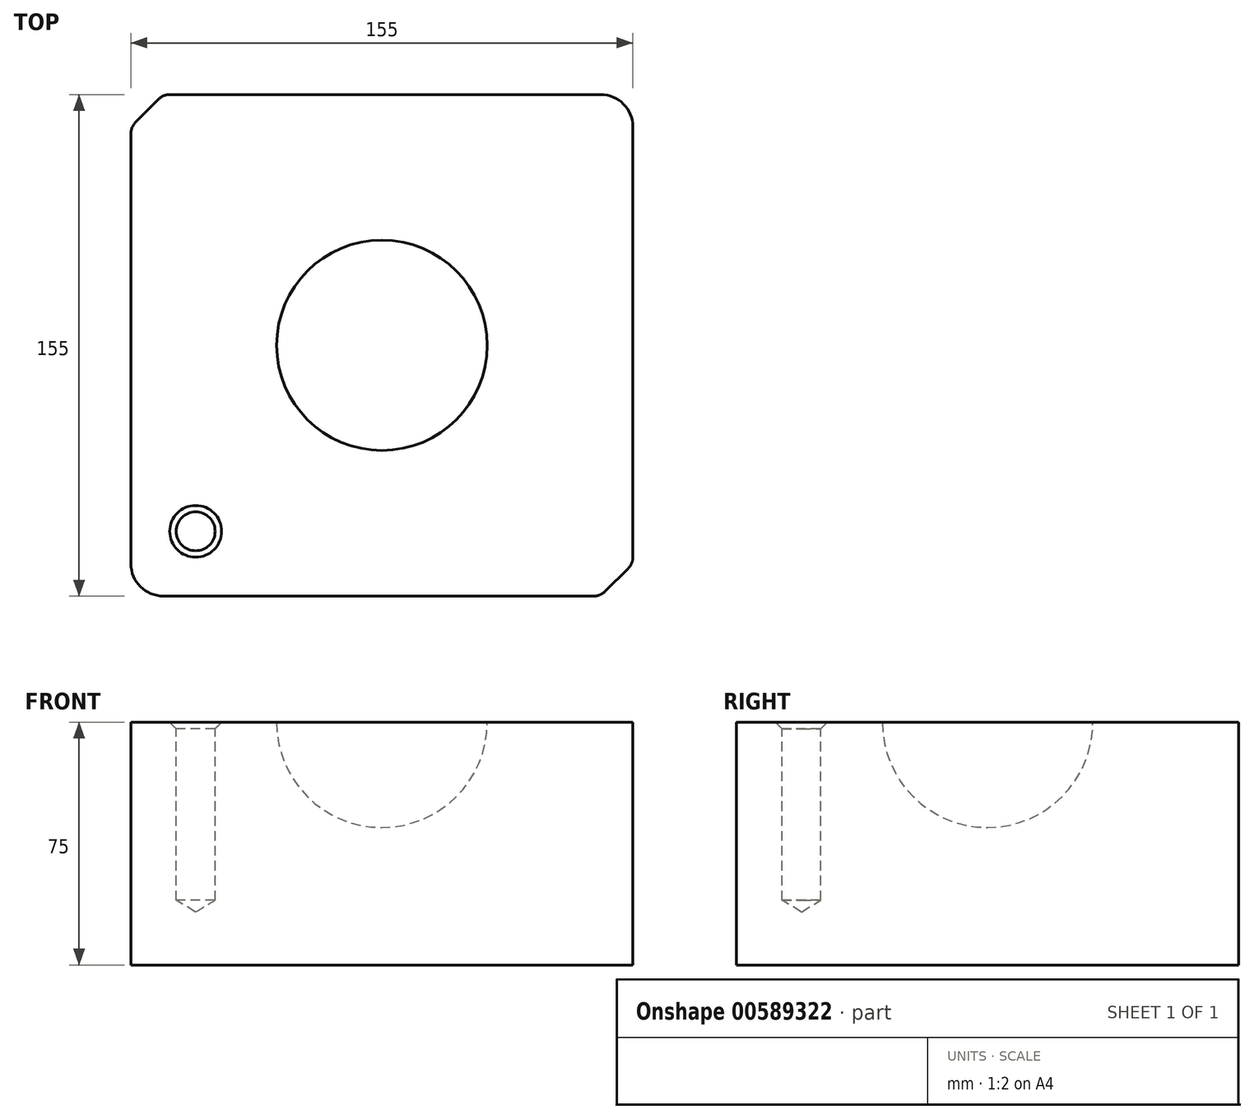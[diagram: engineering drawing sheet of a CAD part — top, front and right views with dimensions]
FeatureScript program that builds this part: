
annotation { "Feature Type Name" : "Feature", "Feature Type Description" : "" }
export const myFeature = defineFeature(function(context is Context, id is Id, definition is map)
    precondition{}
    {
        {
            var Q0;
            Q0=qCreatedBy(makeId("Top.planeOp"),FACE);
            var sketch = newSketch(context, id + "F0", { "sketchPlane" : qUnion([Q0])});
            skLineSegment(sketch, "E0.bottom", {"start": v(77.5, -77.5) * mm, "end": v(-77.5, -77.5) * mm});
            skLineSegment(sketch, "E0.top", {"start": v(77.5, 77.5) * mm, "end": v(-77.5, 77.5) * mm});
            skLineSegment(sketch, "E0.left", {"start": v(77.5, -77.5) * mm, "end": v(77.5, 77.5) * mm});
            skLineSegment(sketch, "E0.right", {"start": v(-77.5, -77.5) * mm, "end": v(-77.5, 77.5) * mm});
            skPoint(sketch, "E0.middle", {"position": v(0, 0) * mm});
            skSolve(sketch);
        }
        {
            var Q0;
            Q0=makeQuery(id+"F0.imprint","IMPRINT",FACE,{"disambiguationData":[TD([[makeQuery(id+"F0.imprint","IMPRINT",EDGE,{"derivedFrom":sQuery(id+"F0.wireOp",EDGE,"E0.bottom")}),-1.0]])]});
            extrude(context, id + "F1", {"entities" : qUnion([Q0]), "depth" : 75 * mm, "offsetDistance" : 25 * mm});
        }
        {
            var Q0;
            Q0=makeQuery(id+"F1.opExtrude","CAP_FACE",FACE,{"disambiguationData":[OSD([sQuery(id+"F0.wireOp",EDGE,"E0.bottom"),sQuery(id+"F0.wireOp",EDGE,"E0.top"),sQuery(id+"F0.wireOp",EDGE,"E0.left"),sQuery(id+"F0.wireOp",EDGE,"E0.right")])],"isStart":false});
            var sketch = newSketch(context, id + "F2", { "sketchPlane" : qUnion([Q0])});
            skCircle(sketch, "E1", {"center": v(0, 0) * mm, "radius": 32.5 * mm});
            skLineSegment(sketch, "E2", {"start": v(0, 37.52) * mm, "end": v(0, -38.72) * mm});
            skSolve(sketch);
        }
        {
            var Q0;
            {var subQ0=sQuery(id+"F2.wireOp",EDGE,"E2");var subQ1=sQuery(id+"F2.wireOp",EDGE,"E1");var subQ2=makeQuery(id+"F2.imprint","INTERSECT",VERTEX,{"disambiguationData":[OD(0.0)],"derivedFrom":[subQ1,subQ0]});Q0=makeQuery(id+"F2.imprint","IMPRINT",FACE,{"disambiguationData":[TD([[makeQuery(id+"F2.imprint","IMPRINT",EDGE,{"disambiguationData":[TD([[subQ2,1.0]])],"derivedFrom":subQ1}),1.0]])]});}
            var Q1;
            Q1=sQuery(id+"F2.wireOp",EDGE,"E2");
            revolve(context, id + "F3", {"operationType" : NewBodyOperationType.REMOVE, "entities" : qUnion([Q0]), "axis" : qUnion([Q1]), "revolveType" : RevolveType.FULL, "oppositeDirection" : true});
        }
        {
            var Q0;
            Q0=makeQuery(id+"F1.opExtrude","CAP_FACE",FACE,{"disambiguationData":[OSD([sQuery(id+"F0.wireOp",EDGE,"E0.bottom"),sQuery(id+"F0.wireOp",EDGE,"E0.top"),sQuery(id+"F0.wireOp",EDGE,"E0.left"),sQuery(id+"F0.wireOp",EDGE,"E0.right")])],"isStart":false});
            var sketch = newSketch(context, id + "F4", { "sketchPlane" : qUnion([Q0])});
            skCircle(sketch, "E3", {"center": v(-57.5, -57.5) * mm, "radius": 8 * mm});
            skSolve(sketch);
        }
        {
            var Q0;
            Q0=sQuery(id+"F4.wireOp",VERTEX,"E3.center");
            var Q1;
            Q1=makeQuery(id+"F1.opExtrude","SWEPT_BODY",BODY,{"disambiguationData":[OSD([sQuery(id+"F0.wireOp",EDGE,"E0.bottom"),sQuery(id+"F0.wireOp",EDGE,"E0.top"),sQuery(id+"F0.wireOp",EDGE,"E0.left"),sQuery(id+"F0.wireOp",EDGE,"E0.right")])]});
            hole(context, id + "F5", {"style" : HoleStyle.C_SINK, "endStyle" : HoleEndStyle.BLIND, "holeDiameter" : 12 * mm, "cSinkDiameter" : 16 * mm, "cSinkAngle" : 90 * degree, "majorDiameter" : 5 * mm, "holeDepth" : 55 * mm, "isTappedThrough" : true, "tappedDepth" : 12 * mm, "tapClearance" : 3, "locations" : qUnion([Q0]), "scope" : qUnion([Q1])});
        }
        {
            var Q0;
            Q0=makeQuery(id+"F1.opExtrude","CAP_VERTEX",VERTEX,{"disambiguationData":[OSD([sQuery(id+"F0.wireOp",EDGE,"E0.top"),sQuery(id+"F0.wireOp",EDGE,"E0.right")])],"isStart":false});
            var Q1;
            Q1=makeQuery(id+"F1.opExtrude","CAP_VERTEX",VERTEX,{"disambiguationData":[OSD([sQuery(id+"F0.wireOp",EDGE,"E0.bottom"),sQuery(id+"F0.wireOp",EDGE,"E0.left")])],"isStart":true});
            var Q2;
            Q2=makeQuery(id+"F1.opExtrude","CAP_VERTEX",VERTEX,{"disambiguationData":[OSD([sQuery(id+"F0.wireOp",EDGE,"E0.bottom"),sQuery(id+"F0.wireOp",EDGE,"E0.left")])],"isStart":false});
            cPlane(context, id + "F6", {"entities" : qUnion([Q0, Q1, Q2]), "cplaneType" : CPlaneType.THREE_POINT, "offset" : 25 * mm, "width" : 150 * mm, "height" : 150 * mm});
        }
        {
            var Q0;
            Q0=makeQuery(id+"F1.opExtrude","SWEPT_EDGE",EDGE,{"disambiguationData":[OSD([sQuery(id+"F0.wireOp",EDGE,"E0.bottom"),sQuery(id+"F0.wireOp",EDGE,"E0.right")])]});
            var Q1;
            Q1=makeQuery(id+"F1.opExtrude","SWEPT_EDGE",EDGE,{"disambiguationData":[OSD([sQuery(id+"F0.wireOp",EDGE,"E0.top"),sQuery(id+"F0.wireOp",EDGE,"E0.left")])]});
            fillet(context, id + "F7", {"entities" : qUnion([Q0, Q1]), "radius" : 10 * mm, "tangentPropagation" : true, "allowEdgeOverflow" : false});
        }
        {
            var Q0;
            Q0=makeQuery(id+"F1.opExtrude","SWEPT_EDGE",EDGE,{"disambiguationData":[OSD([sQuery(id+"F0.wireOp",EDGE,"E0.top"),sQuery(id+"F0.wireOp",EDGE,"E0.right")])]});
            var Q1;
            Q1=makeQuery(id+"F1.opExtrude","SWEPT_EDGE",EDGE,{"disambiguationData":[OSD([sQuery(id+"F0.wireOp",EDGE,"E0.bottom"),sQuery(id+"F0.wireOp",EDGE,"E0.left")])]});
            chamfer(context, id + "F8", {"entities" : qUnion([Q0, Q1]), "width" : 10 * mm, "tangentPropagation" : true});
        }
        {
            var Q0;
            {var subQ0=sQuery(id+"F0.wireOp",EDGE,"E0.right");Q0=makeQuery(id+"F8.opChamfer","BLEND_EDGE",EDGE,{"blendedFrom":[makeQuery(id+"F1.opExtrude","SWEPT_EDGE",EDGE,{"disambiguationData":[OSD([sQuery(id+"F0.wireOp",EDGE,"E0.top"),subQ0])]}),makeQuery(id+"F1.opExtrude","SWEPT_FACE",FACE,{"disambiguationData":[OSD([subQ0])]})],"blendedInto":[makeQuery(id+"F1.opExtrude","SWEPT_FACE",FACE,{"disambiguationData":[OSD([subQ0])]})]});}
            var Q1;
            {var subQ0=sQuery(id+"F0.wireOp",EDGE,"E0.top");Q1=makeQuery(id+"F8.opChamfer","BLEND_EDGE",EDGE,{"blendedFrom":[makeQuery(id+"F1.opExtrude","SWEPT_EDGE",EDGE,{"disambiguationData":[OSD([subQ0,sQuery(id+"F0.wireOp",EDGE,"E0.right")])]}),makeQuery(id+"F1.opExtrude","SWEPT_FACE",FACE,{"disambiguationData":[OSD([subQ0])]})],"blendedInto":[makeQuery(id+"F1.opExtrude","SWEPT_FACE",FACE,{"disambiguationData":[OSD([subQ0])]})]});}
            var Q2;
            {var subQ0=sQuery(id+"F0.wireOp",EDGE,"E0.bottom");Q2=makeQuery(id+"F8.opChamfer","BLEND_EDGE",EDGE,{"blendedFrom":[makeQuery(id+"F1.opExtrude","SWEPT_EDGE",EDGE,{"disambiguationData":[OSD([subQ0,sQuery(id+"F0.wireOp",EDGE,"E0.left")])]}),makeQuery(id+"F1.opExtrude","SWEPT_FACE",FACE,{"disambiguationData":[OSD([subQ0])]})],"blendedInto":[makeQuery(id+"F1.opExtrude","SWEPT_FACE",FACE,{"disambiguationData":[OSD([subQ0])]})]});}
            var Q3;
            {var subQ0=sQuery(id+"F0.wireOp",EDGE,"E0.left");Q3=makeQuery(id+"F8.opChamfer","BLEND_EDGE",EDGE,{"blendedFrom":[makeQuery(id+"F1.opExtrude","SWEPT_EDGE",EDGE,{"disambiguationData":[OSD([sQuery(id+"F0.wireOp",EDGE,"E0.bottom"),subQ0])]}),makeQuery(id+"F1.opExtrude","SWEPT_FACE",FACE,{"disambiguationData":[OSD([subQ0])]})],"blendedInto":[makeQuery(id+"F1.opExtrude","SWEPT_FACE",FACE,{"disambiguationData":[OSD([subQ0])]})]});}
            fillet(context, id + "F9", {"entities" : qUnion([Q0, Q1, Q2, Q3]), "radius" : 5 * mm, "tangentPropagation" : true, "allowEdgeOverflow" : false});
        }
    });
